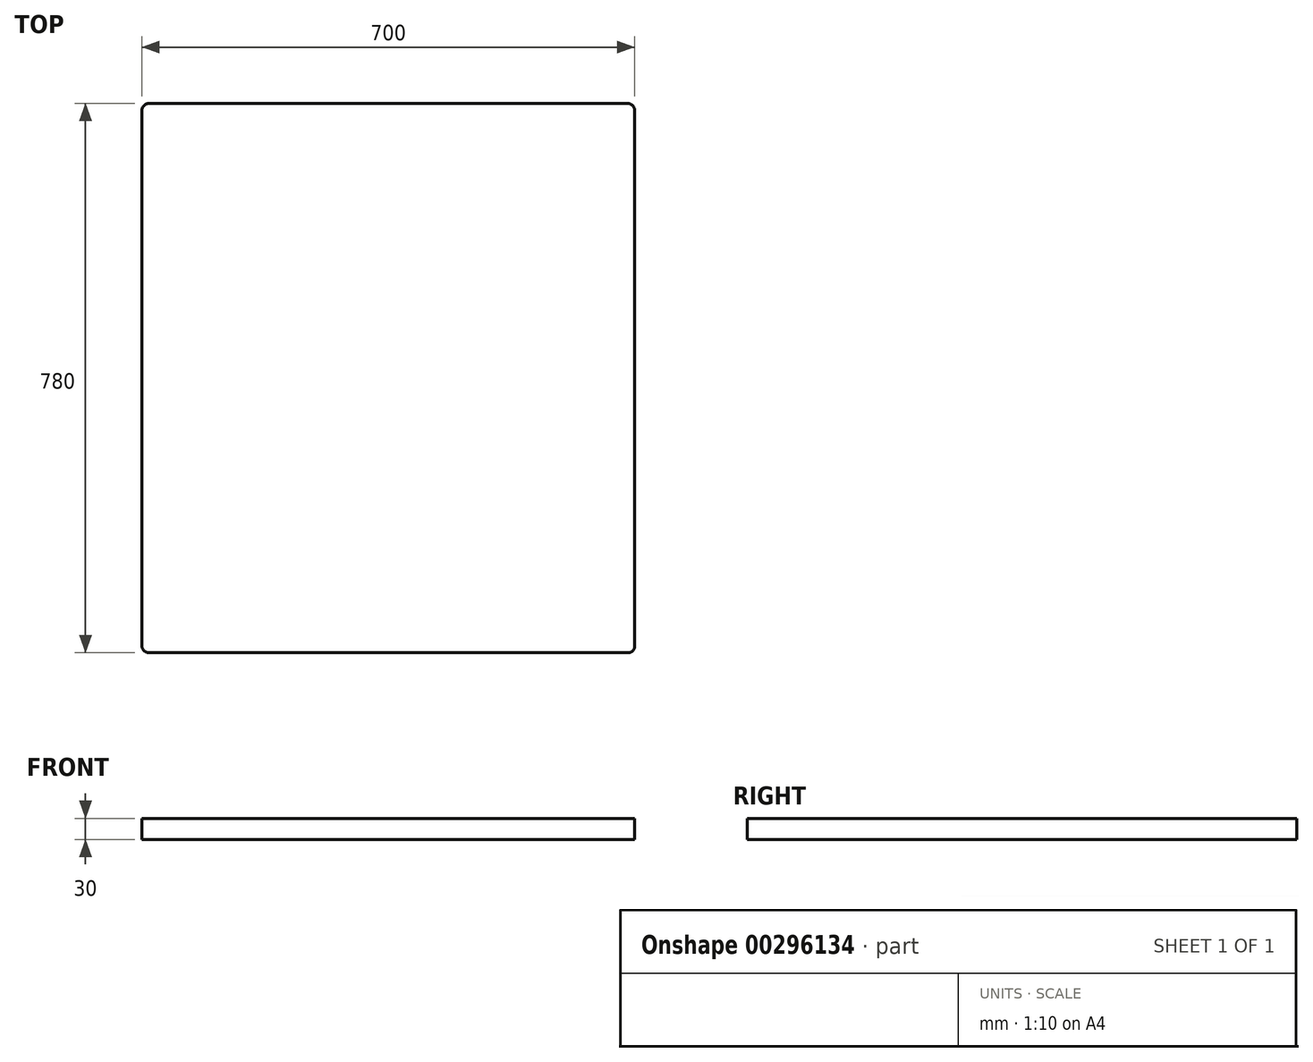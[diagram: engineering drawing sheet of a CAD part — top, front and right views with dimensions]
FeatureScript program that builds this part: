
annotation { "Feature Type Name" : "Feature", "Feature Type Description" : "" }
export const myFeature = defineFeature(function(context is Context, id is Id, definition is map)
    precondition{}
    {
        {
            var Q0;
            Q0=qCreatedBy(makeId("Top.planeOp"),FACE);
            var sketch = newSketch(context, id + "F0", { "sketchPlane" : qUnion([Q0])});
            skLineSegment(sketch, "E0.bottom", {"start": v(340, 390) * mm, "end": v(-340, 390) * mm});
            skLineSegment(sketch, "E0.top", {"start": v(340, -390) * mm, "end": v(-340, -390) * mm});
            skLineSegment(sketch, "E0.left", {"start": v(350, 380) * mm, "end": v(350, -380) * mm});
            skLineSegment(sketch, "E0.right", {"start": v(-350, 380) * mm, "end": v(-350, -380) * mm});
            skPoint(sketch, "E0.middle", {"position": v(0, 0) * mm});
            skPoint(sketch, "E1.visualSharp", {"position": v(-350, 390) * mm});
            skArc(sketch, "E1.filletArc", {"start": v(-340, 390) * mm, "mid": v(-347.07, 387.07) * mm, "end": v(-350, 380) * mm});
            skPoint(sketch, "E2.visualSharp", {"position": v(350, 390) * mm});
            skArc(sketch, "E2.filletArc", {"start": v(350, 380) * mm, "mid": v(347.07, 387.07) * mm, "end": v(340, 390) * mm});
            skPoint(sketch, "E3.visualSharp", {"position": v(350, -390) * mm});
            skArc(sketch, "E3.filletArc", {"start": v(340, -390) * mm, "mid": v(347.07, -387.07) * mm, "end": v(350, -380) * mm});
            skPoint(sketch, "E4.visualSharp", {"position": v(-350, -390) * mm});
            skArc(sketch, "E4.filletArc", {"start": v(-350, -380) * mm, "mid": v(-347.07, -387.07) * mm, "end": v(-340, -390) * mm});
            skSolve(sketch);
        }
        {
            var Q0;
            Q0=makeQuery(id+"F0.imprint","IMPRINT",FACE,{"disambiguationData":[TD([[makeQuery(id+"F0.imprint","IMPRINT",EDGE,{"derivedFrom":sQuery(id+"F0.wireOp",EDGE,"E0.bottom")}),1.0]])]});
            extrude(context, id + "F1", {"entities" : qUnion([Q0]), "oppositeDirection" : true, "depth" : 30 * mm});
        }
    });
